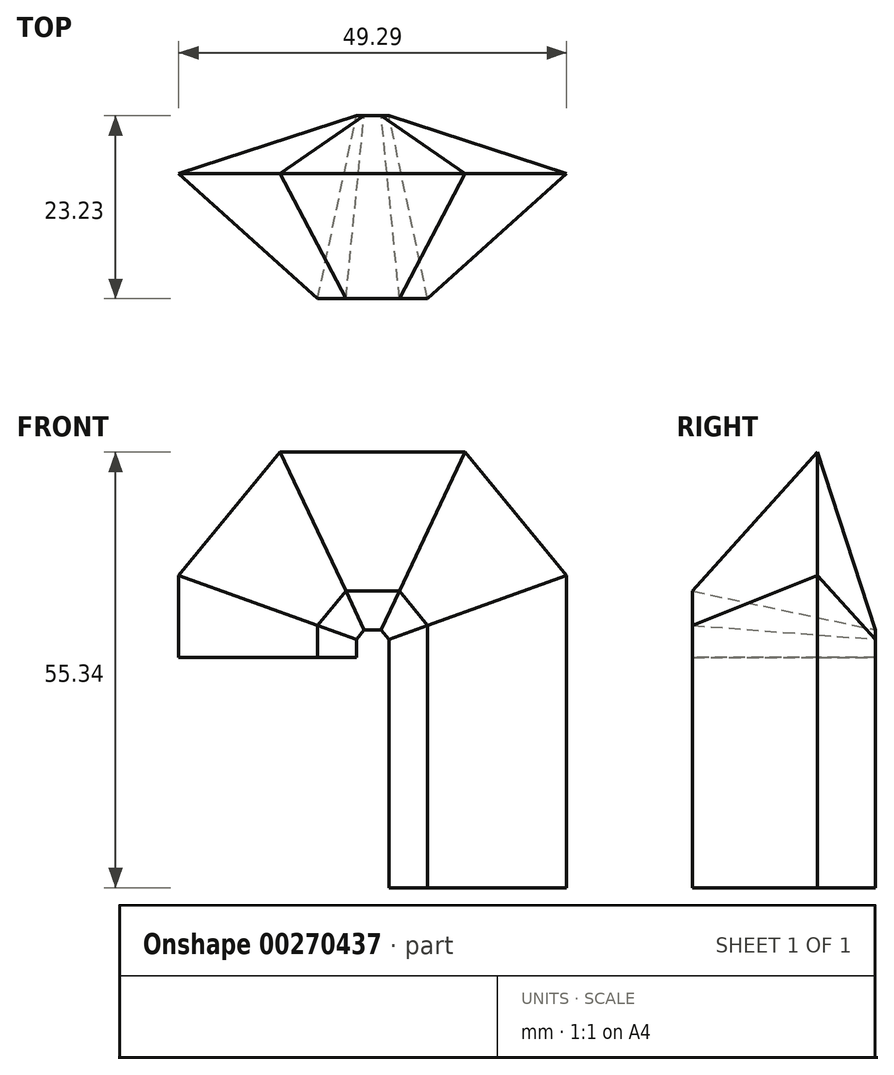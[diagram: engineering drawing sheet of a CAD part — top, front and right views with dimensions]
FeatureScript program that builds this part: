
annotation { "Feature Type Name" : "Feature", "Feature Type Description" : "" }
export const myFeature = defineFeature(function(context is Context, id is Id, definition is map)
    precondition{}
    {
        {
            var Q0;
            Q0=qCreatedBy(makeId("Front.planeOp"),FACE);
            var sketch = newSketch(context, id + "F0", { "sketchPlane" : qUnion([Q0])});
            skLineSegment(sketch, "E0", {"start": v(0, 0) * mm, "end": v(0, 34.85) * mm});
            skLineSegment(sketch, "E1", {"start": v(0, 34.85) * mm, "end": v(-5.83, 41.93) * mm});
            skLineSegment(sketch, "E2", {"start": v(-5.83, 41.93) * mm, "end": v(-16.65, 41.93) * mm});
            skLineSegment(sketch, "E3", {"start": v(-16.65, 41.93) * mm, "end": v(-22.47, 34.85) * mm});
            skLineSegment(sketch, "E4", {"start": v(-22.47, 34.85) * mm, "end": v(-22.47, 29.24) * mm});
            skSolve(sketch);
        }
        {
            var Q0;
            Q0=qCreatedBy(makeId("Top.planeOp"),FACE);
            var sketch = newSketch(context, id + "F1", { "sketchPlane" : qUnion([Q0])});
            skCircle(sketch, "E5.cCircle", {"center": v(0, 0) * mm, "radius": 6.85 * mm, "construction": true});
            skLineSegment(sketch, "E5.0", {"start": v(13.4, 2.83) * mm, "end": v(-4.25, -13.03) * mm});
            skLineSegment(sketch, "E5.1", {"start": v(-4.25, -13.03) * mm, "end": v(-9.16, 10.2) * mm});
            skLineSegment(sketch, "E5.2", {"start": v(-9.16, 10.2) * mm, "end": v(13.4, 2.83) * mm});
            skPoint(sketch, "E5.0.midPoint", {"position": v(4.58, -5.1) * mm});
            skSolve(sketch);
        }
        {
            var Q0;
            Q0=makeQuery(id+"F1.imprint","IMPRINT",FACE,{"disambiguationData":[TD([[makeQuery(id+"F1.imprint","IMPRINT",EDGE,{"derivedFrom":sQuery(id+"F1.wireOp",EDGE,"E5.0")}),-1.0]])]});
            var Q1;
            Q1=sQuery(id+"F0.wireOp",EDGE,"E0");
            var Q2;
            Q2=sQuery(id+"F0.wireOp",EDGE,"E1");
            var Q3;
            Q3=sQuery(id+"F0.wireOp",EDGE,"E2");
            var Q4;
            Q4=sQuery(id+"F0.wireOp",EDGE,"E3");
            var Q5;
            Q5=sQuery(id+"F0.wireOp",EDGE,"E4");
            sweep(context, id + "F2", {"profiles" : qUnion([Q0]), "path" : qUnion([Q1, Q2, Q3, Q4, Q5])});
        }
    });
